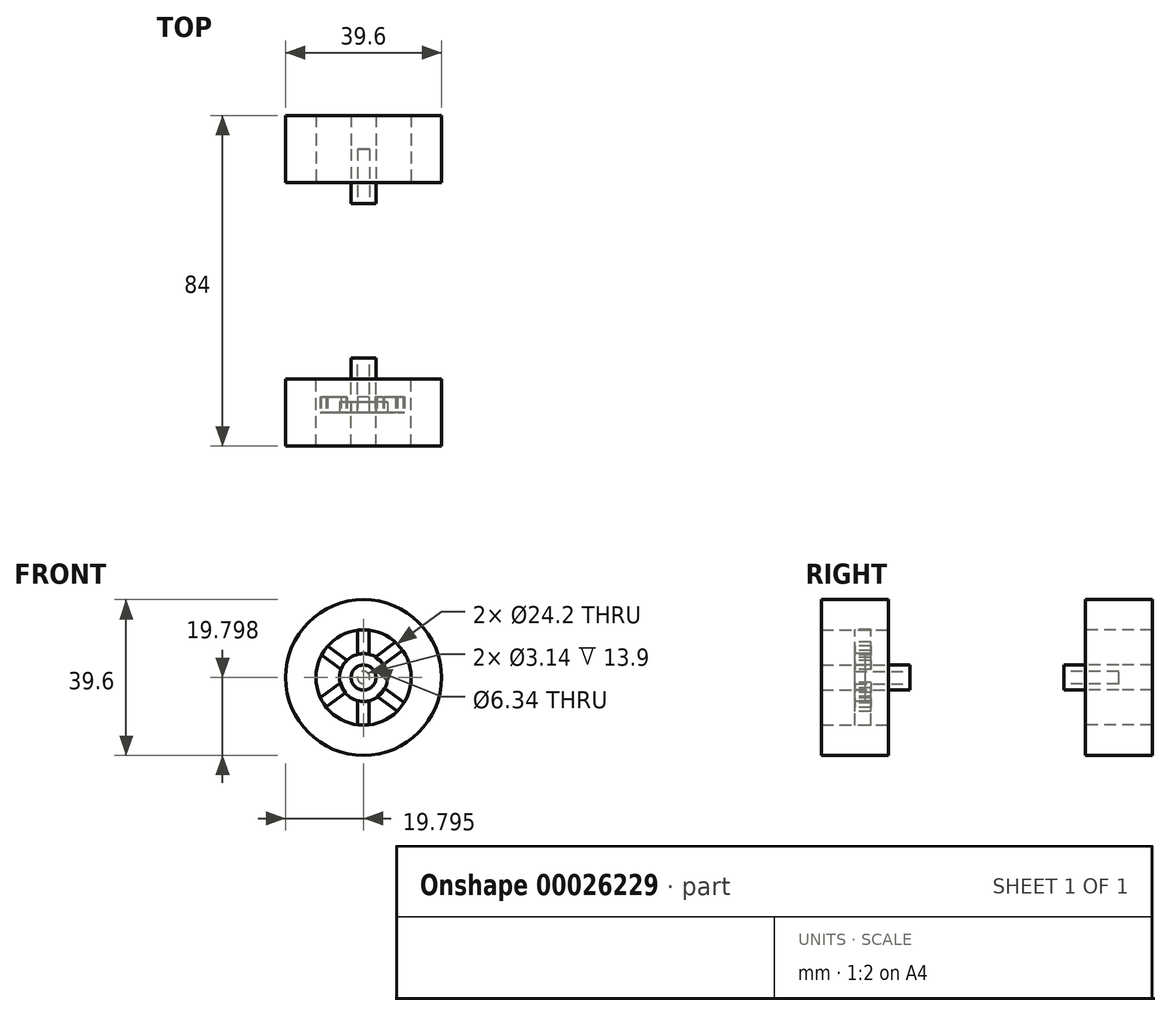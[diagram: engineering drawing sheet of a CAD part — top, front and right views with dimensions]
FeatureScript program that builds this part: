
annotation { "Feature Type Name" : "Feature", "Feature Type Description" : "" }
export const myFeature = defineFeature(function(context is Context, id is Id, definition is map)
    precondition{}
    {
        {
            var Q0;
            Q0=qCreatedBy(makeId("Front.planeOp"),FACE);
            var sketch = newSketch(context, id + "F0", { "sketchPlane" : qUnion([Q0])});
            skCircle(sketch, "E0", {"center": v(-14.5, -5.85) * mm, "radius": 3.17 * mm});
            skCircle(sketch, "E1.0", {"center": v(-14.5, -5.85) * mm, "radius": 1.57 * mm});
            skSolve(sketch);
        }
        {
            var Q0;
            Q0=makeQuery(id+"F0.imprint","IMPRINT",FACE,{"disambiguationData":[TD([[makeQuery(id+"F0.imprint","IMPRINT",EDGE,{"derivedFrom":sQuery(id+"F0.wireOp",EDGE,"E0")}),1.0]])]});
            extrude(context, id + "F1", {"entities" : qUnion([Q0]), "depth" : 9.2 * mm});
        }
        {
            var Q0;
            Q0=makeQuery(id+"F1.opExtrude","CAP_FACE",FACE,{"disambiguationData":[OSD([sQuery(id+"F0.wireOp",EDGE,"E0"),sQuery(id+"F0.wireOp",EDGE,"E1.0")])],"isStart":false});
            var sketch = newSketch(context, id + "F2", { "sketchPlane" : qUnion([Q0])});
            skCircle(sketch, "E2.0", {"center": v(-14.5, -5.85) * mm, "radius": 6.07 * mm});
            skSolve(sketch);
        }
        {
            var Q0;
            Q0=makeQuery(id+"F2.imprint","IMPRINT",FACE,{"disambiguationData":[TD([[makeQuery(id+"F2.imprint","IMPRINT",EDGE,{"derivedFrom":sQuery(id+"F2.wireOp",EDGE,"E2.0")}),1.0]])]});
            extrude(context, id + "F3", {"entities" : qUnion([Q0]), "oppositeDirection" : true, "depth" : 2.7 * mm});
        }
        {
            var Q0;
            Q0=makeQuery(id+"F3.opExtrude","CAP_FACE",FACE,{"disambiguationData":[OSD([sQuery(id+"F0.wireOp",EDGE,"E0"),sQuery(id+"F2.wireOp",EDGE,"E2.0")])],"isStart":true});
            var sketch = newSketch(context, id + "F4", { "sketchPlane" : qUnion([Q0])});
            skArc(sketch, "E3", {"start": v(-23.66, 2.2) * mm, "mid": v(-24.53, 1.09) * mm, "end": v(-25.26, -0.1) * mm});
            skLineSegment(sketch, "E4", {"start": v(-24.08, -13.4) * mm, "end": v(-19, -9.65) * mm});
            skLineSegment(sketch, "E5.0", {"start": v(-13.15, -18.05) * mm, "end": v(-13.15, -11.58) * mm});
            skLineSegment(sketch, "E6.0", {"start": v(-15.95, -18.05) * mm, "end": v(-15.95, -11.55) * mm});
            skLineSegment(sketch, "E7.0", {"start": v(-4.11, -12.26) * mm, "end": v(-9.23, -8.47) * mm});
            skLineSegment(sketch, "E8.0", {"start": v(-5.85, -14.46) * mm, "end": v(-11.04, -10.62) * mm});
            skLineSegment(sketch, "E9.0", {"start": v(-25.55, -11.01) * mm, "end": v(-20.25, -7.1) * mm});
            skLineSegment(sketch, "E10.trimOffspring", {"start": v(-13.15, -0.13) * mm, "end": v(-13.15, 6.35) * mm});
            skLineSegment(sketch, "E11.trimOffspring", {"start": v(-11.62, -0.72) * mm, "end": v(-6.32, 3.2) * mm});
            skLineSegment(sketch, "E12.trimOffspring", {"start": v(-18.55, -1.59) * mm, "end": v(-23.7, 2.22) * mm});
            skCircle(sketch, "E13", {"center": v(-14.5, -5.85) * mm, "radius": 5.88 * mm});
            skLineSegment(sketch, "E14.trimOffspring", {"start": v(-15.95, -0.15) * mm, "end": v(-15.95, 6.35) * mm});
            skLineSegment(sketch, "E15.trimOffspring", {"start": v(-20.06, -3.95) * mm, "end": v(-25.36, -0.03) * mm});
            skLineSegment(sketch, "E16.trimOffspring", {"start": v(-9.55, -2.67) * mm, "end": v(-4.46, 1.1) * mm});
            skArc(sketch, "E17.trimOffspring", {"start": v(-13.15, 6.27) * mm, "mid": v(-14.55, 6.35) * mm, "end": v(-15.95, 6.26) * mm});
            skArc(sketch, "E18.trimOffspring", {"start": v(-4.46, 1.1) * mm, "mid": v(-5.33, 2.2) * mm, "end": v(-6.32, 3.2) * mm});
            skArc(sketch, "E19.trimOffspring", {"start": v(-5.85, -14.46) * mm, "mid": v(-4.92, -13.4) * mm, "end": v(-4.11, -12.26) * mm});
            skArc(sketch, "E20.trimOffspring", {"start": v(-15.95, -17.97) * mm, "mid": v(-14.55, -18.05) * mm, "end": v(-13.15, -17.98) * mm});
            skArc(sketch, "E21.trimOffspring", {"start": v(-25.55, -11.01) * mm, "mid": v(-24.88, -12.25) * mm, "end": v(-24.08, -13.4) * mm});
            skSolve(sketch);
        }
        {
            var Q0;
            {var subQ0=sQuery(id+"F4.wireOp",EDGE,"E17.trimOffspring");Q0=makeQuery(id+"F4.imprint","IMPRINT",FACE,{"disambiguationData":[TD([[makeQuery(id+"F4.imprint","IMPRINT",EDGE,{"derivedFrom":subQ0}),1.0]])]});}
            var Q1;
            {var subQ2=sQuery(id+"F4.wireOp",EDGE,"E11.trimOffspring");Q1=makeQuery(id+"F4.imprint","IMPRINT",FACE,{"disambiguationData":[TD([[makeQuery(id+"F4.imprint","IMPRINT",EDGE,{"derivedFrom":subQ2}),-1.0]])]});}
            var Q2;
            {var subQ2=sQuery(id+"F4.wireOp",EDGE,"E7.0");Q2=makeQuery(id+"F4.imprint","IMPRINT",FACE,{"disambiguationData":[TD([[makeQuery(id+"F4.imprint","IMPRINT",EDGE,{"derivedFrom":subQ2}),1.0]])]});}
            var Q3;
            {var subQ0=sQuery(id+"F4.wireOp",EDGE,"E20.trimOffspring");Q3=makeQuery(id+"F4.imprint","IMPRINT",FACE,{"disambiguationData":[TD([[makeQuery(id+"F4.imprint","IMPRINT",EDGE,{"derivedFrom":subQ0}),1.0]])]});}
            var Q4;
            {var subQ3=sQuery(id+"F4.wireOp",EDGE,"E3");Q4=makeQuery(id+"F4.imprint","IMPRINT",FACE,{"disambiguationData":[TD([[makeQuery(id+"F4.imprint","IMPRINT",EDGE,{"derivedFrom":subQ3}),1.0]])]});}
            var Q5;
            {var subQ2=sQuery(id+"F4.wireOp",EDGE,"E4");Q5=makeQuery(id+"F4.imprint","IMPRINT",FACE,{"disambiguationData":[TD([[makeQuery(id+"F4.imprint","IMPRINT",EDGE,{"derivedFrom":subQ2}),1.0]])]});}
            extrude(context, id + "F5", {"entities" : qUnion([Q0, Q1, Q2, Q3, Q4, Q5]), "oppositeDirection" : true, "depth" : 4 * mm});
        }
        {
            var Q0;
            Q0=makeQuery(id+"F1.opExtrude","CAP_FACE",FACE,{"disambiguationData":[OSD([sQuery(id+"F0.wireOp",EDGE,"E0"),sQuery(id+"F0.wireOp",EDGE,"E1.0")])],"isStart":false});
            var sketch = newSketch(context, id + "F6", { "sketchPlane" : qUnion([Q0])});
            skCircle(sketch, "E22", {"center": v(-14.5, -5.85) * mm, "radius": 12.1 * mm});
            skCircle(sketch, "E23.0", {"center": v(-14.5, -5.85) * mm, "radius": 19.8 * mm});
            skSolve(sketch);
        }
        {
            var Q0;
            Q0=makeQuery(id+"F6.imprint","IMPRINT",FACE,{"disambiguationData":[TD([[makeQuery(id+"F6.imprint","IMPRINT",EDGE,{"derivedFrom":sQuery(id+"F6.wireOp",EDGE,"E22")}),-1.0]])]});
            extrude(context, id + "F7", {"entities" : qUnion([Q0]), "depth" : 17 * mm, "symmetric" : true});
        }
        {
            var Q0;
            Q0=makeQuery(id+"F1.opExtrude","CAP_FACE",FACE,{"disambiguationData":[OSD([sQuery(id+"F0.wireOp",EDGE,"E0"),sQuery(id+"F0.wireOp",EDGE,"E1.0")])],"isStart":true});
            extrude(context, id + "F8", {"entities" : qUnion([Q0]), "operationType" : NewBodyOperationType.ADD, "depth" : 4.7 * mm});
        }
        {
            var Q0;
            Q0=makeQuery(id+"F1.opExtrude","CAP_FACE",FACE,{"disambiguationData":[OSD([sQuery(id+"F0.wireOp",EDGE,"E0"),sQuery(id+"F0.wireOp",EDGE,"E1.0")])],"isStart":false});
            var sketch = newSketch(context, id + "F9", { "sketchPlane" : qUnion([Q0])});
            skCircle(sketch, "E24", {"center": v(-14.5, -5.85) * mm, "radius": 3.16 * mm});
            skSolve(sketch);
        }
        {
            var Q0;
            Q0=qSketchRegion(id+"F9",true);
            var Q1;
            Q1=makeQuery(id+"F7.opExtrude","CAP_FACE",FACE,{"disambiguationData":[OSD([sQuery(id+"F6.wireOp",EDGE,"E22"),sQuery(id+"F6.wireOp",EDGE,"E23.0")])],"isStart":false});
            extrude(context, id + "F10", {"entities" : qUnion([Q0]), "operationType" : NewBodyOperationType.ADD, "endBound" : BoundingType.UP_TO_SURFACE, "endBoundEntityFace" : qUnion([Q1]), "depth" : 25 * mm});
        }
        {
            var Q0;
            Q0=makeQuery(id+"F10.opExtrude","CAP_FACE",FACE,{"disambiguationData":[OSD([sQuery(id+"F9.wireOp",EDGE,"E24")])],"isStart":false});
            extrude(context, id + "F11", {"entities" : qUnion([Q0]), "operationType" : NewBodyOperationType.ADD, "oppositeDirection" : true, "depth" : 3 * mm});
        }
        {
            var Q0;
            Q0=makeQuery(id+"F7.opExtrude","SWEPT_BODY",BODY,{"disambiguationData":[OSD([sQuery(id+"F6.wireOp",EDGE,"E22"),sQuery(id+"F6.wireOp",EDGE,"E23.0")])]});
            var Q1;
            Q1=makeQuery(id+"F1.opExtrude","SWEPT_BODY",BODY,{"disambiguationData":[OSD([sQuery(id+"F0.wireOp",EDGE,"E0"),sQuery(id+"F0.wireOp",EDGE,"E1.0")])]});
            var Q2;
            Q2=makeQuery(id+"F7.opExtrude","CAP_FACE",FACE,{"disambiguationData":[OSD([sQuery(id+"F6.wireOp",EDGE,"E22"),sQuery(id+"F6.wireOp",EDGE,"E23.0")])],"isStart":true});
            mirror(context, id + "F12", {"entities" : qUnion([Q0, Q1]), "mirrorPlane" : qUnion([Q2])});
        }
        {
            var Q0;
            Q0=makeQuery(id+"F12.opPattern","COPY",BODY,{"derivedFrom":makeQuery(id+"F1.opExtrude","SWEPT_BODY",BODY,{"disambiguationData":[OSD([sQuery(id+"F0.wireOp",EDGE,"E0"),sQuery(id+"F0.wireOp",EDGE,"E1.0")])]}),"instanceName":"1"});
            var Q1;
            Q1=makeQuery(id+"F12.opPattern","COPY",BODY,{"derivedFrom":makeQuery(id+"F7.opExtrude","SWEPT_BODY",BODY,{"disambiguationData":[OSD([sQuery(id+"F6.wireOp",EDGE,"E22"),sQuery(id+"F6.wireOp",EDGE,"E23.0")])]}),"instanceName":"1"});
            var Q2;
            Q2=makeQuery(id+"F12.opPattern","COPY",FACE,{"derivedFrom":makeQuery(id+"F10.opExtrude","SWEPT_FACE",FACE,{"disambiguationData":[OSD([sQuery(id+"F9.wireOp",EDGE,"E24")])]}),"instanceName":"1"});
            transform(context, id + "F13", {"entities" : qUnion([Q0, Q1]), "transformType" : TransformType.TRANSLATION_DISTANCE, "transformDirection" : qUnion([Q2]), "distance" : 50 * mm, "oppositeDirection" : true, "makeCopy" : false});
        }
    });
